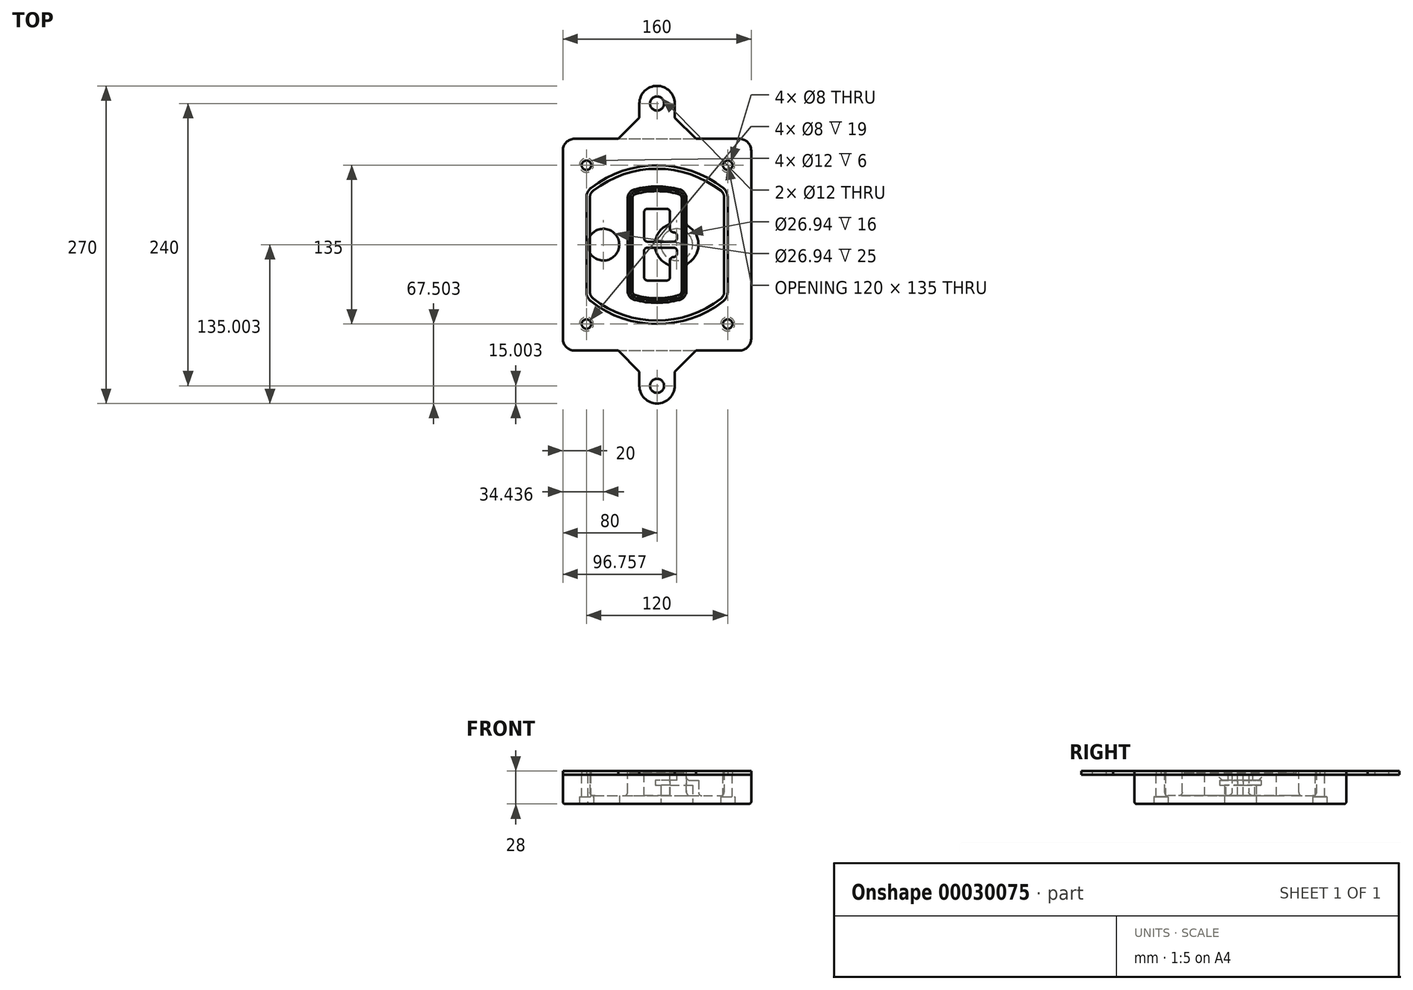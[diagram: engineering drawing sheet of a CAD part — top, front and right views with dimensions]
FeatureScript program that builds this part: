
annotation { "Feature Type Name" : "Feature", "Feature Type Description" : "" }
export const myFeature = defineFeature(function(context is Context, id is Id, definition is map)
    precondition{}
    {
        {
            var Q0;
            Q0=qCreatedBy(makeId("Top.planeOp"),FACE);
            var sketch = newSketch(context, id + "F0", { "sketchPlane" : qUnion([Q0])});
            skPoint(sketch, "E0.rect.middle", {"position": v(0, 0) * mm});
            skLineSegment(sketch, "E1.bottom", {"start": v(24.05, 28.38) * mm, "end": v(164.05, 28.38) * mm});
            skLineSegment(sketch, "E1.top", {"start": v(24.05, 208.38) * mm, "end": v(164.05, 208.38) * mm});
            skLineSegment(sketch, "E1.left", {"start": v(14.05, 38.38) * mm, "end": v(14.05, 198.38) * mm});
            skLineSegment(sketch, "E1.right", {"start": v(174.05, 38.38) * mm, "end": v(174.05, 198.38) * mm});
            skLineSegment(sketch, "E2", {"start": v(14.05, 208.38) * mm, "end": v(174.05, 28.38) * mm, "construction": true});
            skLineSegment(sketch, "E3", {"start": v(174.05, 208.38) * mm, "end": v(14.05, 28.38) * mm, "construction": true});
            skCircle(sketch, "E4", {"center": v(34.05, 185.88) * mm, "radius": 4 * mm});
            skCircle(sketch, "E5", {"center": v(154.05, 185.88) * mm, "radius": 4 * mm});
            skCircle(sketch, "E6", {"center": v(154.05, 50.88) * mm, "radius": 4 * mm});
            skCircle(sketch, "E7", {"center": v(34.05, 50.88) * mm, "radius": 4 * mm});
            skLineSegment(sketch, "E8", {"start": v(34.05, 185.88) * mm, "end": v(154.05, 185.88) * mm, "construction": true});
            skLineSegment(sketch, "E9", {"start": v(154.05, 185.88) * mm, "end": v(154.05, 50.88) * mm, "construction": true});
            skLineSegment(sketch, "E10", {"start": v(154.05, 50.88) * mm, "end": v(34.05, 50.88) * mm, "construction": true});
            skLineSegment(sketch, "E11", {"start": v(34.05, 50.88) * mm, "end": v(34.05, 185.88) * mm, "construction": true});
            skLineSegment(sketch, "E12", {"start": v(34.05, 158.68) * mm, "end": v(34.05, 78.09) * mm});
            skLineSegment(sketch, "E13", {"start": v(154.05, 158.68) * mm, "end": v(154.05, 78.09) * mm});
            skArc(sketch, "E14", {"start": v(150.2, 166.56) * mm, "mid": v(94.05, 185.88) * mm, "end": v(37.9, 166.56) * mm});
            skArc(sketch, "E15", {"start": v(37.9, 70.2) * mm, "mid": v(94.05, 50.88) * mm, "end": v(150.2, 70.2) * mm});
            skLineSegment(sketch, "E16", {"start": v(34.05, 118.38) * mm, "end": v(154.05, 118.38) * mm, "construction": true});
            skPoint(sketch, "E17.visualSharp", {"position": v(34.05, 73.38) * mm});
            skArc(sketch, "E17.filletArc", {"start": v(34.05, 78.09) * mm, "mid": v(35.06, 73.7) * mm, "end": v(37.9, 70.2) * mm});
            skPoint(sketch, "E18.visualSharp", {"position": v(34.05, 163.38) * mm});
            skArc(sketch, "E18.filletArc", {"start": v(37.9, 166.56) * mm, "mid": v(35.06, 163.06) * mm, "end": v(34.05, 158.68) * mm});
            skPoint(sketch, "E19.visualSharp", {"position": v(154.05, 163.38) * mm});
            skArc(sketch, "E19.filletArc", {"start": v(154.05, 158.68) * mm, "mid": v(153.04, 163.06) * mm, "end": v(150.2, 166.56) * mm});
            skPoint(sketch, "E20.visualSharp", {"position": v(154.05, 73.38) * mm});
            skArc(sketch, "E20.filletArc", {"start": v(150.2, 70.2) * mm, "mid": v(153.04, 73.7) * mm, "end": v(154.05, 78.09) * mm});
            skPoint(sketch, "E21.visualSharp", {"position": v(14.05, 208.38) * mm});
            skArc(sketch, "E21.filletArc", {"start": v(24.05, 208.38) * mm, "mid": v(16.98, 205.45) * mm, "end": v(14.05, 198.38) * mm});
            skPoint(sketch, "E22.visualSharp", {"position": v(174.05, 208.38) * mm});
            skArc(sketch, "E22.filletArc", {"start": v(174.05, 198.38) * mm, "mid": v(171.12, 205.45) * mm, "end": v(164.05, 208.38) * mm});
            skPoint(sketch, "E23.visualSharp", {"position": v(174.05, 28.38) * mm});
            skArc(sketch, "E23.filletArc", {"start": v(164.05, 28.38) * mm, "mid": v(171.12, 31.31) * mm, "end": v(174.05, 38.38) * mm});
            skPoint(sketch, "E24.visualSharp", {"position": v(14.05, 28.38) * mm});
            skArc(sketch, "E24.filletArc", {"start": v(14.05, 38.38) * mm, "mid": v(16.98, 31.31) * mm, "end": v(24.05, 28.38) * mm});
            skArc(sketch, "E25.0", {"start": v(151.05, 158.68) * mm, "mid": v(150.34, 161.75) * mm, "end": v(148.36, 164.2) * mm});
            skLineSegment(sketch, "E25.1", {"start": v(151.05, 158.68) * mm, "end": v(151.05, 78.09) * mm});
            skArc(sketch, "E25.2", {"start": v(148.36, 72.57) * mm, "mid": v(150.34, 75.02) * mm, "end": v(151.05, 78.09) * mm});
            skArc(sketch, "E25.3", {"start": v(39.74, 72.57) * mm, "mid": v(94.05, 53.88) * mm, "end": v(148.36, 72.57) * mm});
            skArc(sketch, "E25.4", {"start": v(37.05, 78.09) * mm, "mid": v(37.76, 75.02) * mm, "end": v(39.74, 72.57) * mm});
            skArc(sketch, "E25.5", {"start": v(148.36, 164.2) * mm, "mid": v(94.05, 182.88) * mm, "end": v(39.74, 164.2) * mm});
            skLineSegment(sketch, "E25.6", {"start": v(37.05, 158.68) * mm, "end": v(37.05, 78.09) * mm});
            skArc(sketch, "E25.7", {"start": v(39.74, 164.2) * mm, "mid": v(37.76, 161.75) * mm, "end": v(37.05, 158.68) * mm});
            skArc(sketch, "E26.0", {"start": v(35.43, 169.71) * mm, "mid": v(31.47, 164.82) * mm, "end": v(30.05, 158.68) * mm});
            skArc(sketch, "E26.1", {"start": v(152.67, 169.71) * mm, "mid": v(94.05, 189.88) * mm, "end": v(35.43, 169.71) * mm});
            skArc(sketch, "E26.2", {"start": v(158.05, 158.68) * mm, "mid": v(156.63, 164.82) * mm, "end": v(152.67, 169.71) * mm});
            skLineSegment(sketch, "E26.3", {"start": v(158.05, 158.68) * mm, "end": v(158.05, 78.09) * mm});
            skArc(sketch, "E26.4", {"start": v(152.67, 67.05) * mm, "mid": v(156.63, 71.95) * mm, "end": v(158.05, 78.09) * mm});
            skLineSegment(sketch, "E26.5", {"start": v(30.05, 158.68) * mm, "end": v(30.05, 78.09) * mm});
            skArc(sketch, "E26.6", {"start": v(35.43, 67.05) * mm, "mid": v(94.05, 46.88) * mm, "end": v(152.67, 67.05) * mm});
            skArc(sketch, "E26.7", {"start": v(30.05, 78.09) * mm, "mid": v(31.47, 71.95) * mm, "end": v(35.43, 67.05) * mm});
            skSolve(sketch);
        }
        {
            var Q0;
            Q0=makeQuery(id+"F0.imprint","IMPRINT",FACE,{"disambiguationData":[TD([[makeQuery(id+"F0.imprint","IMPRINT",EDGE,{"derivedFrom":sQuery(id+"F0.wireOp",EDGE,"E1.bottom")}),1.0]])]});
            var Q1;
            Q1=makeQuery(id+"F0.imprint","IMPRINT",FACE,{"disambiguationData":[TD([[makeQuery(id+"F0.imprint","IMPRINT",EDGE,{"derivedFrom":sQuery(id+"F0.wireOp",EDGE,"E12")}),1.0]])]});
            var Q2;
            Q2=makeQuery(id+"F0.imprint","IMPRINT",FACE,{"disambiguationData":[TD([[makeQuery(id+"F0.imprint","IMPRINT",EDGE,{"derivedFrom":sQuery(id+"F0.wireOp",EDGE,"E25.0")}),1.0]])]});
            var Q3;
            Q3=makeQuery(id+"F0.imprint","IMPRINT",FACE,{"disambiguationData":[TD([[makeQuery(id+"F0.imprint","IMPRINT",EDGE,{"derivedFrom":sQuery(id+"F0.wireOp",EDGE,"E12")}),-1.0]])]});
            extrude(context, id + "F1", {"entities" : qUnion([Q0, Q1, Q2, Q3]), "oppositeDirection" : true, "depth" : 25 * mm});
        }
        {
            var Q0;
            Q0=makeQuery(id+"F0.imprint","IMPRINT",FACE,{"disambiguationData":[TD([[makeQuery(id+"F0.imprint","IMPRINT",EDGE,{"derivedFrom":sQuery(id+"F0.wireOp",EDGE,"E12")}),1.0]])]});
            extrude(context, id + "F2", {"entities" : qUnion([Q0]), "operationType" : NewBodyOperationType.ADD, "depth" : 3 * mm});
        }
        {
            var Q0;
            Q0=makeQuery(id+"F0.imprint","IMPRINT",FACE,{"disambiguationData":[TD([[makeQuery(id+"F0.imprint","IMPRINT",EDGE,{"derivedFrom":sQuery(id+"F0.wireOp",EDGE,"E25.0")}),1.0]])]});
            extrude(context, id + "F3", {"entities" : qUnion([Q0]), "operationType" : NewBodyOperationType.REMOVE, "oppositeDirection" : true, "depth" : 18 * mm});
        }
        {
            var Q0;
            Q0=makeQuery(id+"F2.opExtrude","CAP_FACE",FACE,{"disambiguationData":[OSD([sQuery(id+"F0.wireOp",EDGE,"E12"),sQuery(id+"F0.wireOp",EDGE,"E13"),sQuery(id+"F0.wireOp",EDGE,"E14"),sQuery(id+"F0.wireOp",EDGE,"E15"),sQuery(id+"F0.wireOp",EDGE,"E17.filletArc"),sQuery(id+"F0.wireOp",EDGE,"E18.filletArc"),sQuery(id+"F0.wireOp",EDGE,"E19.filletArc"),sQuery(id+"F0.wireOp",EDGE,"E20.filletArc"),sQuery(id+"F0.wireOp",EDGE,"E25.0"),sQuery(id+"F0.wireOp",EDGE,"E25.1"),sQuery(id+"F0.wireOp",EDGE,"E25.2"),sQuery(id+"F0.wireOp",EDGE,"E25.3"),sQuery(id+"F0.wireOp",EDGE,"E25.4"),sQuery(id+"F0.wireOp",EDGE,"E25.5"),sQuery(id+"F0.wireOp",EDGE,"E25.6"),sQuery(id+"F0.wireOp",EDGE,"E25.7")])],"isStart":false});
            var sketch = newSketch(context, id + "F4", { "sketchPlane" : qUnion([Q0])});
            skArc(sketch, "E27.0", {"start": v(74.97, 71.41) * mm, "mid": v(94.05, 68.88) * mm, "end": v(113.13, 71.41) * mm});
            skArc(sketch, "E28.0", {"start": v(113.13, 165.35) * mm, "mid": v(94.05, 167.88) * mm, "end": v(74.97, 165.35) * mm});
            skLineSegment(sketch, "E29", {"start": v(69.05, 157.63) * mm, "end": v(69.05, 79.14) * mm});
            skLineSegment(sketch, "E30", {"start": v(119.05, 157.63) * mm, "end": v(119.05, 79.14) * mm});
            skLineSegment(sketch, "E31", {"start": v(69.05, 163.48) * mm, "end": v(119.05, 163.48) * mm, "construction": true});
            skLineSegment(sketch, "E32", {"start": v(69.05, 73.28) * mm, "end": v(119.05, 73.28) * mm, "construction": true});
            skPoint(sketch, "E33.visualSharp", {"position": v(69.05, 163.48) * mm});
            skArc(sketch, "E33.filletArc", {"start": v(74.97, 165.35) * mm, "mid": v(70.7, 162.5) * mm, "end": v(69.05, 157.63) * mm});
            skPoint(sketch, "E34.visualSharp", {"position": v(119.05, 163.48) * mm});
            skArc(sketch, "E34.filletArc", {"start": v(119.05, 157.63) * mm, "mid": v(117.4, 162.5) * mm, "end": v(113.13, 165.35) * mm});
            skPoint(sketch, "E35.visualSharp", {"position": v(119.05, 73.28) * mm});
            skArc(sketch, "E35.filletArc", {"start": v(113.13, 71.41) * mm, "mid": v(117.4, 74.27) * mm, "end": v(119.05, 79.14) * mm});
            skPoint(sketch, "E36.visualSharp", {"position": v(69.05, 73.28) * mm});
            skArc(sketch, "E36.filletArc", {"start": v(69.05, 79.14) * mm, "mid": v(70.7, 74.27) * mm, "end": v(74.97, 71.41) * mm});
            skArc(sketch, "E37.0", {"start": v(148.36, 164.2) * mm, "mid": v(94.05, 182.88) * mm, "end": v(39.74, 164.2) * mm});
            skArc(sketch, "E37.1", {"start": v(39.74, 164.2) * mm, "mid": v(37.76, 161.75) * mm, "end": v(37.05, 158.68) * mm});
            skLineSegment(sketch, "E37.2", {"start": v(37.05, 158.68) * mm, "end": v(37.05, 78.09) * mm});
            skArc(sketch, "E37.3", {"start": v(37.05, 78.09) * mm, "mid": v(37.76, 75.02) * mm, "end": v(39.74, 72.57) * mm});
            skArc(sketch, "E37.4", {"start": v(39.74, 72.57) * mm, "mid": v(94.05, 53.88) * mm, "end": v(148.36, 72.57) * mm});
            skArc(sketch, "E37.5", {"start": v(148.36, 72.57) * mm, "mid": v(150.34, 75.02) * mm, "end": v(151.05, 78.09) * mm});
            skLineSegment(sketch, "E37.6", {"start": v(151.05, 158.68) * mm, "end": v(151.05, 78.09) * mm});
            skArc(sketch, "E37.7", {"start": v(151.05, 158.68) * mm, "mid": v(150.34, 161.75) * mm, "end": v(148.36, 164.2) * mm});
            skLineSegment(sketch, "E38.0", {"start": v(117.05, 157.63) * mm, "end": v(117.05, 79.14) * mm});
            skArc(sketch, "E38.1", {"start": v(112.61, 73.34) * mm, "mid": v(115.81, 75.49) * mm, "end": v(117.05, 79.14) * mm});
            skArc(sketch, "E38.2", {"start": v(75.49, 73.34) * mm, "mid": v(94.05, 70.88) * mm, "end": v(112.61, 73.34) * mm});
            skArc(sketch, "E38.3", {"start": v(71.05, 79.14) * mm, "mid": v(72.29, 75.49) * mm, "end": v(75.49, 73.34) * mm});
            skLineSegment(sketch, "E38.4", {"start": v(71.05, 157.63) * mm, "end": v(71.05, 79.14) * mm});
            skArc(sketch, "E38.5", {"start": v(117.05, 157.63) * mm, "mid": v(115.81, 161.28) * mm, "end": v(112.61, 163.42) * mm});
            skArc(sketch, "E38.6", {"start": v(75.49, 163.42) * mm, "mid": v(72.29, 161.28) * mm, "end": v(71.05, 157.63) * mm});
            skArc(sketch, "E38.7", {"start": v(112.61, 163.42) * mm, "mid": v(94.05, 165.88) * mm, "end": v(75.49, 163.42) * mm});
            skArc(sketch, "E39.0", {"start": v(115.05, 157.63) * mm, "mid": v(114.23, 160.06) * mm, "end": v(112.1, 161.5) * mm});
            skLineSegment(sketch, "E39.1", {"start": v(115.05, 157.63) * mm, "end": v(115.05, 79.14) * mm});
            skArc(sketch, "E39.2", {"start": v(112.1, 75.27) * mm, "mid": v(114.23, 76.7) * mm, "end": v(115.05, 79.14) * mm});
            skArc(sketch, "E39.3", {"start": v(76, 75.27) * mm, "mid": v(94.05, 72.88) * mm, "end": v(112.1, 75.27) * mm});
            skArc(sketch, "E39.4", {"start": v(73.05, 79.14) * mm, "mid": v(73.87, 76.7) * mm, "end": v(76, 75.27) * mm});
            skArc(sketch, "E39.5", {"start": v(112.1, 161.5) * mm, "mid": v(94.05, 163.88) * mm, "end": v(76, 161.5) * mm});
            skLineSegment(sketch, "E39.6", {"start": v(73.05, 157.63) * mm, "end": v(73.05, 79.14) * mm});
            skArc(sketch, "E39.7", {"start": v(76, 161.5) * mm, "mid": v(73.87, 160.06) * mm, "end": v(73.05, 157.63) * mm});
            skLineSegment(sketch, "E40", {"start": v(69.05, 118.38) * mm, "end": v(119.05, 118.38) * mm, "construction": true});
            skLineSegment(sketch, "E41", {"start": v(83.05, 123.88) * mm, "end": v(83.05, 145.88) * mm});
            skLineSegment(sketch, "E42", {"start": v(86.05, 148.88) * mm, "end": v(102.05, 148.88) * mm});
            skLineSegment(sketch, "E43", {"start": v(105.05, 145.88) * mm, "end": v(105.05, 131.88) * mm});
            skLineSegment(sketch, "E44", {"start": v(108.05, 128.88) * mm, "end": v(108.05, 128.88) * mm});
            skLineSegment(sketch, "E45", {"start": v(111.05, 125.88) * mm, "end": v(111.05, 123.88) * mm});
            skLineSegment(sketch, "E46", {"start": v(108.05, 120.88) * mm, "end": v(86.05, 120.88) * mm});
            skPoint(sketch, "E47.visualSharp", {"position": v(83.05, 148.88) * mm});
            skArc(sketch, "E47.filletArc", {"start": v(86.05, 148.88) * mm, "mid": v(83.93, 148) * mm, "end": v(83.05, 145.88) * mm});
            skPoint(sketch, "E48.visualSharp", {"position": v(105.05, 148.88) * mm});
            skArc(sketch, "E48.filletArc", {"start": v(105.05, 145.88) * mm, "mid": v(104.17, 148) * mm, "end": v(102.05, 148.88) * mm});
            skPoint(sketch, "E49.visualSharp", {"position": v(105.05, 128.88) * mm});
            skArc(sketch, "E49.filletArc", {"start": v(105.05, 131.88) * mm, "mid": v(105.93, 129.76) * mm, "end": v(108.05, 128.88) * mm});
            skPoint(sketch, "E50.visualSharp", {"position": v(111.05, 128.88) * mm});
            skArc(sketch, "E50.filletArc", {"start": v(111.05, 125.88) * mm, "mid": v(110.17, 128) * mm, "end": v(108.05, 128.88) * mm});
            skPoint(sketch, "E51.visualSharp", {"position": v(111.05, 120.88) * mm});
            skArc(sketch, "E51.filletArc", {"start": v(108.05, 120.88) * mm, "mid": v(110.17, 121.76) * mm, "end": v(111.05, 123.88) * mm});
            skPoint(sketch, "E52.visualSharp", {"position": v(83.05, 120.88) * mm});
            skArc(sketch, "E52.filletArc", {"start": v(83.05, 123.88) * mm, "mid": v(83.93, 121.76) * mm, "end": v(86.05, 120.88) * mm});
            skLineSegment(sketch, "E53.0.MirrorCS", {"start": v(108.05, 115.88) * mm, "end": v(86.05, 115.88) * mm});
            skArc(sketch, "E54.0.MirrorCS", {"start": v(83.05, 112.88) * mm, "mid": v(83.93, 115) * mm, "end": v(86.05, 115.88) * mm});
            skLineSegment(sketch, "E55.0.MirrorCS", {"start": v(83.05, 112.88) * mm, "end": v(83.05, 90.88) * mm});
            skArc(sketch, "E56.0.MirrorCS", {"start": v(86.05, 87.88) * mm, "mid": v(83.93, 88.76) * mm, "end": v(83.05, 90.88) * mm});
            skLineSegment(sketch, "E57.0.MirrorCS", {"start": v(86.05, 87.88) * mm, "end": v(102.05, 87.88) * mm});
            skArc(sketch, "E58.0.MirrorCS", {"start": v(105.05, 90.88) * mm, "mid": v(104.17, 88.76) * mm, "end": v(102.05, 87.88) * mm});
            skLineSegment(sketch, "E59.0.MirrorCS", {"start": v(105.05, 90.88) * mm, "end": v(105.05, 104.88) * mm});
            skArc(sketch, "E60.0.MirrorCS", {"start": v(105.05, 104.88) * mm, "mid": v(105.93, 107) * mm, "end": v(108.05, 107.88) * mm});
            skArc(sketch, "E61.0.MirrorCS", {"start": v(111.05, 110.88) * mm, "mid": v(110.17, 108.76) * mm, "end": v(108.05, 107.88) * mm});
            skLineSegment(sketch, "E62.0.MirrorCS", {"start": v(111.05, 110.88) * mm, "end": v(111.05, 112.88) * mm});
            skArc(sketch, "E63.0.MirrorCS", {"start": v(108.05, 115.88) * mm, "mid": v(110.17, 115) * mm, "end": v(111.05, 112.88) * mm});
            skSolve(sketch);
        }
        {
            var Q0;
            Q0=makeQuery(id+"F4.imprint","IMPRINT",FACE,{"disambiguationData":[TD([[makeQuery(id+"F4.imprint","IMPRINT",EDGE,{"derivedFrom":sQuery(id+"F4.wireOp",EDGE,"E27.0")}),1.0]])]});
            var Q1;
            Q1=makeQuery(id+"F4.imprint","IMPRINT",FACE,{"disambiguationData":[TD([[makeQuery(id+"F4.imprint","IMPRINT",EDGE,{"derivedFrom":sQuery(id+"F4.wireOp",EDGE,"E38.0")}),-1.0]])]});
            var Q2;
            Q2=makeQuery(id+"F4.imprint","IMPRINT",FACE,{"disambiguationData":[TD([[makeQuery(id+"F4.imprint","IMPRINT",EDGE,{"derivedFrom":sQuery(id+"F4.wireOp",EDGE,"E39.0")}),1.0]])]});
            extrude(context, id + "F5", {"entities" : qUnion([Q0, Q1, Q2]), "operationType" : NewBodyOperationType.ADD, "endBound" : BoundingType.UP_TO_NEXT, "oppositeDirection" : true, "depth" : 25 * mm});
        }
        {
            var Q0;
            Q0=makeQuery(id+"F4.imprint","IMPRINT",FACE,{"disambiguationData":[TD([[makeQuery(id+"F4.imprint","IMPRINT",EDGE,{"derivedFrom":sQuery(id+"F4.wireOp",EDGE,"E38.0")}),-1.0]])]});
            extrude(context, id + "F6", {"entities" : qUnion([Q0]), "operationType" : NewBodyOperationType.REMOVE, "oppositeDirection" : true, "depth" : 2 * mm});
        }
        {
            var Q0;
            Q0=makeQuery(id+"F1.opExtrude","CAP_FACE",FACE,{"disambiguationData":[OSD([sQuery(id+"F0.wireOp",EDGE,"E1.bottom"),sQuery(id+"F0.wireOp",EDGE,"E1.top"),sQuery(id+"F0.wireOp",EDGE,"E1.left"),sQuery(id+"F0.wireOp",EDGE,"E1.right"),sQuery(id+"F0.wireOp",EDGE,"E4"),sQuery(id+"F0.wireOp",EDGE,"E5"),sQuery(id+"F0.wireOp",EDGE,"E6"),sQuery(id+"F0.wireOp",EDGE,"E7"),sQuery(id+"F0.wireOp",EDGE,"E21.filletArc"),sQuery(id+"F0.wireOp",EDGE,"E22.filletArc"),sQuery(id+"F0.wireOp",EDGE,"E23.filletArc"),sQuery(id+"F0.wireOp",EDGE,"E24.filletArc")])],"isStart":false});
            var sketch = newSketch(context, id + "F7", { "sketchPlane" : qUnion([Q0])});
            skCircle(sketch, "E64", {"center": v(110.8, -118.38) * mm, "radius": 13.47 * mm});
            skCircle(sketch, "E65", {"center": v(48.49, -118.38) * mm, "radius": 13.47 * mm});
            skLineSegment(sketch, "E66", {"start": v(174.05, -118.38) * mm, "end": v(14.05, -118.38) * mm});
            skCircle(sketch, "E67", {"center": v(110.8, -118.38) * mm, "radius": 18.47 * mm});
            skCircle(sketch, "E68", {"center": v(154.05, -185.88) * mm, "radius": 6 * mm});
            skCircle(sketch, "E69", {"center": v(34.05, -185.88) * mm, "radius": 6 * mm});
            skCircle(sketch, "E70", {"center": v(34.05, -50.88) * mm, "radius": 6 * mm});
            skCircle(sketch, "E71", {"center": v(154.05, -50.88) * mm, "radius": 6 * mm});
            skSolve(sketch);
        }
        {
            var Q0;
            {var subQ1=sQuery(id+"F7.wireOp",EDGE,"E66");var subQ4=sQuery(id+"F7.wireOp",EDGE,"E64");var subQ6=makeQuery(id+"F7.imprint","INTERSECT",VERTEX,{"disambiguationData":[OD(0.0)],"derivedFrom":[subQ4,subQ1]});Q0=makeQuery(id+"F7.imprint","IMPRINT",FACE,{"disambiguationData":[TD([[makeQuery(id+"F7.imprint","IMPRINT",EDGE,{"disambiguationData":[TD([[subQ6,-1.0]])],"derivedFrom":subQ4}),-1.0]])]});}
            var Q1;
            {var subQ0=sQuery(id+"F7.wireOp",EDGE,"E66");var subQ1=sQuery(id+"F7.wireOp",EDGE,"E64");var subQ3=makeQuery(id+"F7.imprint","INTERSECT",VERTEX,{"disambiguationData":[OD(0.0)],"derivedFrom":[subQ1,subQ0]});Q1=makeQuery(id+"F7.imprint","IMPRINT",FACE,{"disambiguationData":[TD([[makeQuery(id+"F7.imprint","IMPRINT",EDGE,{"disambiguationData":[TD([[subQ3,-1.0]])],"derivedFrom":subQ1}),1.0]])]});}
            var Q2;
            {var subQ0=sQuery(id+"F7.wireOp",EDGE,"E66");var subQ1=sQuery(id+"F7.wireOp",EDGE,"E64");var subQ3=makeQuery(id+"F7.imprint","INTERSECT",VERTEX,{"disambiguationData":[OD(0.0)],"derivedFrom":[subQ1,subQ0]});Q2=makeQuery(id+"F7.imprint","IMPRINT",FACE,{"disambiguationData":[TD([[makeQuery(id+"F7.imprint","IMPRINT",EDGE,{"disambiguationData":[TD([[subQ3,1.0]])],"derivedFrom":subQ1}),1.0]])]});}
            var Q3;
            {var subQ1=sQuery(id+"F7.wireOp",EDGE,"E66");var subQ4=sQuery(id+"F7.wireOp",EDGE,"E64");var subQ6=makeQuery(id+"F7.imprint","INTERSECT",VERTEX,{"disambiguationData":[OD(0.0)],"derivedFrom":[subQ4,subQ1]});Q3=makeQuery(id+"F7.imprint","IMPRINT",FACE,{"disambiguationData":[TD([[makeQuery(id+"F7.imprint","IMPRINT",EDGE,{"disambiguationData":[TD([[subQ6,1.0]])],"derivedFrom":subQ4}),-1.0]])]});}
            extrude(context, id + "F8", {"entities" : qUnion([Q0, Q1, Q2, Q3]), "operationType" : NewBodyOperationType.ADD, "oppositeDirection" : true, "depth" : 20 * mm});
        }
        {
            var Q0;
            {var subQ0=sQuery(id+"F7.wireOp",EDGE,"E66");var subQ1=sQuery(id+"F7.wireOp",EDGE,"E64");var subQ3=makeQuery(id+"F7.imprint","INTERSECT",VERTEX,{"disambiguationData":[OD(0.0)],"derivedFrom":[subQ1,subQ0]});Q0=makeQuery(id+"F7.imprint","IMPRINT",FACE,{"disambiguationData":[TD([[makeQuery(id+"F7.imprint","IMPRINT",EDGE,{"disambiguationData":[TD([[subQ3,-1.0]])],"derivedFrom":subQ1}),1.0]])]});}
            var Q1;
            {var subQ0=sQuery(id+"F7.wireOp",EDGE,"E66");var subQ1=sQuery(id+"F7.wireOp",EDGE,"E64");var subQ3=makeQuery(id+"F7.imprint","INTERSECT",VERTEX,{"disambiguationData":[OD(0.0)],"derivedFrom":[subQ1,subQ0]});Q1=makeQuery(id+"F7.imprint","IMPRINT",FACE,{"disambiguationData":[TD([[makeQuery(id+"F7.imprint","IMPRINT",EDGE,{"disambiguationData":[TD([[subQ3,1.0]])],"derivedFrom":subQ1}),1.0]])]});}
            extrude(context, id + "F9", {"entities" : qUnion([Q0, Q1]), "operationType" : NewBodyOperationType.REMOVE, "oppositeDirection" : true, "depth" : 16 * mm});
        }
        {
            var Q0;
            {var subQ0=sQuery(id+"F7.wireOp",EDGE,"E66");var subQ1=sQuery(id+"F7.wireOp",EDGE,"E65");var subQ3=makeQuery(id+"F7.imprint","INTERSECT",VERTEX,{"disambiguationData":[OD(0.0)],"derivedFrom":[subQ1,subQ0]});Q0=makeQuery(id+"F7.imprint","IMPRINT",FACE,{"disambiguationData":[TD([[makeQuery(id+"F7.imprint","IMPRINT",EDGE,{"disambiguationData":[TD([[subQ3,-1.0]])],"derivedFrom":subQ1}),1.0]])]});}
            var Q1;
            {var subQ0=sQuery(id+"F7.wireOp",EDGE,"E66");var subQ1=sQuery(id+"F7.wireOp",EDGE,"E65");var subQ3=makeQuery(id+"F7.imprint","INTERSECT",VERTEX,{"disambiguationData":[OD(0.0)],"derivedFrom":[subQ1,subQ0]});Q1=makeQuery(id+"F7.imprint","IMPRINT",FACE,{"disambiguationData":[TD([[makeQuery(id+"F7.imprint","IMPRINT",EDGE,{"disambiguationData":[TD([[subQ3,1.0]])],"derivedFrom":subQ1}),1.0]])]});}
            extrude(context, id + "F10", {"entities" : qUnion([Q0, Q1]), "operationType" : NewBodyOperationType.REMOVE, "oppositeDirection" : true, "depth" : 25 * mm});
        }
        {
            var Q0;
            Q0=makeQuery(id+"F7.imprint","IMPRINT",FACE,{"disambiguationData":[TD([[makeQuery(id+"F7.imprint","IMPRINT",EDGE,{"derivedFrom":sQuery(id+"F7.wireOp",EDGE,"E68")}),1.0]])]});
            var Q1;
            Q1=makeQuery(id+"F7.imprint","IMPRINT",FACE,{"disambiguationData":[TD([[makeQuery(id+"F7.imprint","IMPRINT",EDGE,{"derivedFrom":makeQuery(id+"F1.opExtrude","CAP_EDGE",EDGE,{"disambiguationData":[OSD([sQuery(id+"F0.wireOp",EDGE,"E5")])],"isStart":false})}),-1.0]])]});
            var Q2;
            Q2=makeQuery(id+"F7.imprint","IMPRINT",FACE,{"disambiguationData":[TD([[makeQuery(id+"F7.imprint","IMPRINT",EDGE,{"derivedFrom":sQuery(id+"F7.wireOp",EDGE,"E69")}),1.0]])]});
            var Q3;
            Q3=makeQuery(id+"F7.imprint","IMPRINT",FACE,{"disambiguationData":[TD([[makeQuery(id+"F7.imprint","IMPRINT",EDGE,{"derivedFrom":makeQuery(id+"F1.opExtrude","CAP_EDGE",EDGE,{"disambiguationData":[OSD([sQuery(id+"F0.wireOp",EDGE,"E4")])],"isStart":false})}),-1.0]])]});
            var Q4;
            Q4=makeQuery(id+"F7.imprint","IMPRINT",FACE,{"disambiguationData":[TD([[makeQuery(id+"F7.imprint","IMPRINT",EDGE,{"derivedFrom":sQuery(id+"F7.wireOp",EDGE,"E70")}),1.0]])]});
            var Q5;
            Q5=makeQuery(id+"F7.imprint","IMPRINT",FACE,{"disambiguationData":[TD([[makeQuery(id+"F7.imprint","IMPRINT",EDGE,{"derivedFrom":makeQuery(id+"F1.opExtrude","CAP_EDGE",EDGE,{"disambiguationData":[OSD([sQuery(id+"F0.wireOp",EDGE,"E7")])],"isStart":false})}),-1.0]])]});
            var Q6;
            Q6=makeQuery(id+"F7.imprint","IMPRINT",FACE,{"disambiguationData":[TD([[makeQuery(id+"F7.imprint","IMPRINT",EDGE,{"derivedFrom":sQuery(id+"F7.wireOp",EDGE,"E71")}),1.0]])]});
            var Q7;
            Q7=makeQuery(id+"F7.imprint","IMPRINT",FACE,{"disambiguationData":[TD([[makeQuery(id+"F7.imprint","IMPRINT",EDGE,{"derivedFrom":makeQuery(id+"F1.opExtrude","CAP_EDGE",EDGE,{"disambiguationData":[OSD([sQuery(id+"F0.wireOp",EDGE,"E6")])],"isStart":false})}),-1.0]])]});
            extrude(context, id + "F11", {"entities" : qUnion([Q0, Q1, Q2, Q3, Q4, Q5, Q6, Q7]), "operationType" : NewBodyOperationType.REMOVE, "oppositeDirection" : true, "depth" : 6 * mm});
        }
        {
            var Q0;
            Q0=makeQuery(id+"F9.boolean.opBoolean","COPY",FACE,{"derivedFrom":makeQuery(id+"F9.opExtrude","CAP_FACE",FACE,{"disambiguationData":[OSD([sQuery(id+"F7.wireOp",EDGE,"E64")])],"isStart":false})});
            var sketch = newSketch(context, id + "F12", { "sketchPlane" : qUnion([Q0])});
            skArc(sketch, "E72.0", {"start": v(105.05, -100.83) * mm, "mid": v(96.62, -106.56) * mm, "end": v(92.5, -115.88) * mm});
            skArc(sketch, "E72.1", {"start": v(92.5, -120.88) * mm, "mid": v(96.62, -130.2) * mm, "end": v(105.05, -135.93) * mm});
            skLineSegment(sketch, "E73", {"start": v(92.5, -120.88) * mm, "end": v(108.05, -120.88) * mm});
            skLineSegment(sketch, "E74.0", {"start": v(108.05, -115.88) * mm, "end": v(92.5, -115.88) * mm});
            skArc(sketch, "E74.1", {"start": v(108.05, -115.88) * mm, "mid": v(110.17, -115) * mm, "end": v(111.05, -112.88) * mm});
            skLineSegment(sketch, "E74.2", {"start": v(111.05, -110.88) * mm, "end": v(111.05, -112.88) * mm});
            skArc(sketch, "E74.3", {"start": v(111.05, -110.88) * mm, "mid": v(110.17, -108.76) * mm, "end": v(108.05, -107.88) * mm});
            skArc(sketch, "E74.4", {"start": v(105.05, -104.88) * mm, "mid": v(105.93, -107) * mm, "end": v(108.05, -107.88) * mm});
            skLineSegment(sketch, "E74.5", {"start": v(105.05, -100.83) * mm, "end": v(105.05, -104.88) * mm});
            skLineSegment(sketch, "E74.7", {"start": v(108.05, -120.88) * mm, "end": v(92.5, -120.88) * mm});
            skArc(sketch, "E74.8", {"start": v(108.05, -120.88) * mm, "mid": v(110.17, -121.76) * mm, "end": v(111.05, -123.88) * mm});
            skLineSegment(sketch, "E74.9", {"start": v(111.05, -125.88) * mm, "end": v(111.05, -123.88) * mm});
            skArc(sketch, "E74.10", {"start": v(111.05, -125.88) * mm, "mid": v(110.17, -128) * mm, "end": v(108.05, -128.88) * mm});
            skArc(sketch, "E74.11", {"start": v(105.05, -131.88) * mm, "mid": v(105.93, -129.76) * mm, "end": v(108.05, -128.88) * mm});
            skLineSegment(sketch, "E74.12", {"start": v(105.05, -135.93) * mm, "end": v(105.05, -131.88) * mm});
            skPoint(sketch, "E75.orphan", {"position": v(105.05, -145.88) * mm});
            skPoint(sketch, "E76.orphan", {"position": v(86.05, -120.88) * mm});
            skPoint(sketch, "E77.orphan", {"position": v(86.05, -115.88) * mm});
            skPoint(sketch, "E78.orphan", {"position": v(105.05, -90.88) * mm});
            skSolve(sketch);
        }
        {
            var Q0;
            {var subQ7=sQuery(id+"F12.wireOp",EDGE,"E72.0");var subQ14=sQuery(id+"F12.wireOp",EDGE,"E72.1");var subQ16=sQuery(id+"F12.wireOp",EDGE,"E74.1");var subQ18=sQuery(id+"F12.wireOp",EDGE,"E74.8");Q0=qUnion([makeQuery(id+"F12.imprint","IMPRINT",FACE,{"disambiguationData":[TD([[makeQuery(id+"F12.imprint","IMPRINT",EDGE,{"derivedFrom":subQ7}),1.0]])]}),makeQuery(id+"F12.imprint","IMPRINT",FACE,{"disambiguationData":[TD([[makeQuery(id+"F12.imprint","IMPRINT",EDGE,{"derivedFrom":subQ14}),1.0]])]}),makeQuery(id+"F12.imprint","IMPRINT",FACE,{"disambiguationData":[TD([[makeQuery(id+"F12.imprint","IMPRINT",EDGE,{"derivedFrom":subQ16}),1.0]])]}),makeQuery(id+"F12.imprint","IMPRINT",FACE,{"disambiguationData":[TD([[makeQuery(id+"F12.imprint","IMPRINT",EDGE,{"derivedFrom":subQ18}),-1.0]])]})]);}
            var Q1;
            Q1=makeQuery(id+"F5.boolean.opBoolean","SPLIT",FACE,{"disambiguationData":[TD([makeQuery(id+"F5.opExtrude","SWEPT_FACE",FACE,{"disambiguationData":[OSD([sQuery(id+"F4.wireOp",EDGE,"E41")])]})])],"derivedFrom":makeQuery(id+"F3.boolean.opBoolean","COPY",FACE,{"derivedFrom":makeQuery(id+"F3.opExtrude","CAP_FACE",FACE,{"disambiguationData":[OSD([sQuery(id+"F0.wireOp",EDGE,"E25.0"),sQuery(id+"F0.wireOp",EDGE,"E25.1"),sQuery(id+"F0.wireOp",EDGE,"E25.2"),sQuery(id+"F0.wireOp",EDGE,"E25.3"),sQuery(id+"F0.wireOp",EDGE,"E25.4"),sQuery(id+"F0.wireOp",EDGE,"E25.5"),sQuery(id+"F0.wireOp",EDGE,"E25.6"),sQuery(id+"F0.wireOp",EDGE,"E25.7")])],"isStart":false})})});
            extrude(context, id + "F13", {"entities" : qUnion([Q0]), "operationType" : NewBodyOperationType.REMOVE, "endBound" : BoundingType.UP_TO_SURFACE, "endBoundEntityFace" : qUnion([Q1]), "depth" : 25 * mm});
        }
        {
            var Q0;
            Q0=makeQuery(id+"F3.boolean.opBoolean","COPY",EDGE,{"derivedFrom":makeQuery(id+"F3.opExtrude","CAP_EDGE",EDGE,{"disambiguationData":[OSD([sQuery(id+"F0.wireOp",EDGE,"E25.6")])],"isStart":false})});
            var Q1;
            Q1=makeQuery(id+"F8.boolean.opBoolean","INTERSECT",EDGE,{"derivedFrom":[makeQuery(id+"F5.opExtrude","SWEPT_FACE",FACE,{"disambiguationData":[OSD([sQuery(id+"F4.wireOp",EDGE,"E30")])]}),makeQuery(id+"F8.opExtrude","CAP_FACE",FACE,{"disambiguationData":[OSD([sQuery(id+"F7.wireOp",EDGE,"E67")])],"isStart":false})]});
            var Q2;
            Q2=makeQuery(id+"F8.boolean.opBoolean","INTERSECT",EDGE,{"disambiguationData":[OD(1.0)],"derivedFrom":[makeQuery(id+"F5.opExtrude","SWEPT_FACE",FACE,{"disambiguationData":[OSD([sQuery(id+"F4.wireOp",EDGE,"E30")])]}),makeQuery(id+"F8.opExtrude","SWEPT_FACE",FACE,{"disambiguationData":[OSD([sQuery(id+"F7.wireOp",EDGE,"E67")])]})]});
            var Q3;
            {var subQ0=sQuery(id+"F4.wireOp",EDGE,"E30");Q3=makeQuery(id+"F8.boolean.opBoolean","SPLIT",EDGE,{"disambiguationData":[TD([makeQuery(id+"F5.opExtrude","SWEPT_FACE",FACE,{"disambiguationData":[OSD([sQuery(id+"F4.wireOp",EDGE,"E35.filletArc")])]})])],"derivedFrom":makeQuery(id+"F5.opExtrude","CAP_EDGE",EDGE,{"disambiguationData":[OSD([subQ0])],"isStart":false})});}
            var Q4;
            {var subQ0=sQuery(id+"F0.wireOp",EDGE,"E25.7");var subQ1=sQuery(id+"F0.wireOp",EDGE,"E25.1");var subQ2=sQuery(id+"F0.wireOp",EDGE,"E25.6");var subQ3=sQuery(id+"F0.wireOp",EDGE,"E25.5");var subQ4=sQuery(id+"F0.wireOp",EDGE,"E25.4");var subQ5=sQuery(id+"F0.wireOp",EDGE,"E25.0");var subQ6=sQuery(id+"F0.wireOp",EDGE,"E25.2");var subQ7=sQuery(id+"F0.wireOp",EDGE,"E25.3");Q4=makeQuery(id+"F8.boolean.opBoolean","INTERSECT",EDGE,{"derivedFrom":[makeQuery(id+"F5.boolean.opBoolean","SPLIT",FACE,{"disambiguationData":[TD([makeQuery(id+"F2.opExtrude","SWEPT_FACE",FACE,{"disambiguationData":[OSD([subQ5])]})])],"derivedFrom":makeQuery(id+"F3.boolean.opBoolean","COPY",FACE,{"derivedFrom":makeQuery(id+"F3.opExtrude","CAP_FACE",FACE,{"disambiguationData":[OSD([subQ5,subQ1,subQ6,subQ7,subQ4,subQ3,subQ2,subQ0])],"isStart":false})})}),makeQuery(id+"F8.opExtrude","SWEPT_FACE",FACE,{"disambiguationData":[OSD([sQuery(id+"F7.wireOp",EDGE,"E67")])]})]});}
            var Q5;
            Q5=makeQuery(id+"F8.boolean.opBoolean","INTERSECT",EDGE,{"disambiguationData":[OD(0.0)],"derivedFrom":[makeQuery(id+"F5.opExtrude","SWEPT_FACE",FACE,{"disambiguationData":[OSD([sQuery(id+"F4.wireOp",EDGE,"E30")])]}),makeQuery(id+"F8.opExtrude","SWEPT_FACE",FACE,{"disambiguationData":[OSD([sQuery(id+"F7.wireOp",EDGE,"E67")])]})]});
            fillet(context, id + "F14", {"entities" : qUnion([Q0, Q1, Q2, Q3, Q4, Q5]), "radius" : 3 * mm, "tangentPropagation" : true, "allowEdgeOverflow" : false});
        }
        {
            var Q0;
            Q0=makeQuery(id+"F1.opExtrude","CAP_EDGE",EDGE,{"disambiguationData":[OSD([sQuery(id+"F0.wireOp",EDGE,"E1.bottom")])],"isStart":false});
            fillet(context, id + "F15", {"entities" : qUnion([Q0]), "radius" : 2 * mm, "tangentPropagation" : true, "allowEdgeOverflow" : false});
        }
        {
            var Q0;
            {var subQ0=sQuery(id+"F0.wireOp",EDGE,"E1.bottom");var subQ1=sQuery(id+"F0.wireOp",EDGE,"E1.top");var subQ2=sQuery(id+"F0.wireOp",EDGE,"E1.left");var subQ3=sQuery(id+"F0.wireOp",EDGE,"E1.right");var subQ4=sQuery(id+"F0.wireOp",EDGE,"E4");var subQ5=sQuery(id+"F0.wireOp",EDGE,"E5");var subQ6=sQuery(id+"F0.wireOp",EDGE,"E6");var subQ7=sQuery(id+"F0.wireOp",EDGE,"E7");var subQ8=sQuery(id+"F0.wireOp",EDGE,"E21.filletArc");var subQ9=sQuery(id+"F0.wireOp",EDGE,"E22.filletArc");var subQ10=sQuery(id+"F0.wireOp",EDGE,"E23.filletArc");var subQ11=sQuery(id+"F0.wireOp",EDGE,"E24.filletArc");Q0=makeQuery(id+"F2.boolean.opBoolean","SPLIT",FACE,{"disambiguationData":[TD([makeQuery(id+"F1.opExtrude","SWEPT_FACE",FACE,{"disambiguationData":[OSD([subQ0])]})])],"derivedFrom":makeQuery(id+"F1.opExtrude","CAP_FACE",FACE,{"disambiguationData":[OSD([subQ0,subQ1,subQ2,subQ3,subQ4,subQ5,subQ6,subQ7,subQ8,subQ9,subQ10,subQ11])],"isStart":true})});}
            var sketch = newSketch(context, id + "F16", { "sketchPlane" : qUnion([Q0])});
            skLineSegment(sketch, "E79.0", {"start": v(24.05, 208.38) * mm, "end": v(164.05, 208.38) * mm});
            skArc(sketch, "E79.1", {"start": v(174.05, 198.38) * mm, "mid": v(171.12, 205.45) * mm, "end": v(164.05, 208.38) * mm});
            skLineSegment(sketch, "E79.2", {"start": v(174.05, 38.38) * mm, "end": v(174.05, 198.38) * mm});
            skArc(sketch, "E79.3", {"start": v(164.05, 28.38) * mm, "mid": v(171.12, 31.31) * mm, "end": v(174.05, 38.38) * mm});
            skLineSegment(sketch, "E79.4", {"start": v(24.05, 28.38) * mm, "end": v(164.05, 28.38) * mm});
            skArc(sketch, "E79.5", {"start": v(14.05, 38.38) * mm, "mid": v(16.98, 31.31) * mm, "end": v(24.05, 28.38) * mm});
            skLineSegment(sketch, "E79.6", {"start": v(14.05, 38.38) * mm, "end": v(14.05, 198.38) * mm});
            skArc(sketch, "E79.7", {"start": v(24.05, 208.38) * mm, "mid": v(16.98, 205.45) * mm, "end": v(14.05, 198.38) * mm});
            skCircle(sketch, "E79.8", {"center": v(34.05, 185.88) * mm, "radius": 4 * mm});
            skCircle(sketch, "E79.9", {"center": v(154.05, 185.88) * mm, "radius": 4 * mm});
            skCircle(sketch, "E79.10", {"center": v(154.05, 50.88) * mm, "radius": 4 * mm});
            skCircle(sketch, "E79.11", {"center": v(34.05, 50.88) * mm, "radius": 4 * mm});
            skLineSegment(sketch, "E79.12", {"start": v(154.05, 158.68) * mm, "end": v(154.05, 78.09) * mm});
            skArc(sketch, "E79.13", {"start": v(150.2, 70.2) * mm, "mid": v(153.04, 73.7) * mm, "end": v(154.05, 78.09) * mm});
            skArc(sketch, "E79.14", {"start": v(37.9, 70.2) * mm, "mid": v(94.05, 50.88) * mm, "end": v(150.2, 70.2) * mm});
            skArc(sketch, "E79.15", {"start": v(154.05, 158.68) * mm, "mid": v(153.04, 163.06) * mm, "end": v(150.2, 166.56) * mm});
            skArc(sketch, "E79.16", {"start": v(34.05, 78.09) * mm, "mid": v(35.06, 73.7) * mm, "end": v(37.9, 70.2) * mm});
            skLineSegment(sketch, "E79.17", {"start": v(34.05, 158.68) * mm, "end": v(34.05, 78.09) * mm});
            skArc(sketch, "E79.18", {"start": v(37.9, 166.56) * mm, "mid": v(35.06, 163.06) * mm, "end": v(34.05, 158.68) * mm});
            skArc(sketch, "E79.19", {"start": v(150.2, 166.56) * mm, "mid": v(94.05, 185.88) * mm, "end": v(37.9, 166.56) * mm});
            skLineSegment(sketch, "E80", {"start": v(94.05, 208.38) * mm, "end": v(94.05, 238.38) * mm, "construction": true});
            skCircle(sketch, "E81", {"center": v(94.05, 238.38) * mm, "radius": 6 * mm});
            skLineSegment(sketch, "E82", {"start": v(79.05, 238.38) * mm, "end": v(79.05, 226.38) * mm});
            skLineSegment(sketch, "E83", {"start": v(79.05, 226.38) * mm, "end": v(61.05, 208.38) * mm});
            skLineSegment(sketch, "E84", {"start": v(109.05, 238.38) * mm, "end": v(109.05, 226.38) * mm});
            skLineSegment(sketch, "E85", {"start": v(109.05, 226.38) * mm, "end": v(127.05, 208.38) * mm});
            skArc(sketch, "E86", {"start": v(109.05, 238.38) * mm, "mid": v(94.05, 253.38) * mm, "end": v(79.05, 238.38) * mm});
            skLineSegment(sketch, "E87", {"start": v(14.05, 118.38) * mm, "end": v(174.05, 118.38) * mm, "construction": true});
            skArc(sketch, "E88.MirrorCS", {"start": v(109.05, -1.62) * mm, "mid": v(94.05, -16.62) * mm, "end": v(79.05, -1.62) * mm});
            skCircle(sketch, "E89.MirrorC", {"center": v(94.05, -1.62) * mm, "radius": 6 * mm});
            skLineSegment(sketch, "E90.MirrorCS", {"start": v(109.05, -1.62) * mm, "end": v(109.05, 10.38) * mm});
            skLineSegment(sketch, "E91.MirrorCS", {"start": v(79.05, -1.62) * mm, "end": v(79.05, 10.38) * mm});
            skLineSegment(sketch, "E92.MirrorCS", {"start": v(94.05, 28.38) * mm, "end": v(94.05, -1.62) * mm});
            skLineSegment(sketch, "E93.MirrorCS", {"start": v(109.05, 10.38) * mm, "end": v(127.05, 28.38) * mm});
            skLineSegment(sketch, "E94.MirrorCS", {"start": v(79.05, 10.38) * mm, "end": v(61.05, 28.38) * mm});
            skSolve(sketch);
        }
        {
            var Q0;
            Q0 = qSketchRegion(id + "F16", true);
            var Q1;
            Q1=makeQuery(id+"F2.opExtrude","CAP_FACE",FACE,{"disambiguationData":[OSD([sQuery(id+"F0.wireOp",EDGE,"E12"),sQuery(id+"F0.wireOp",EDGE,"E13"),sQuery(id+"F0.wireOp",EDGE,"E14"),sQuery(id+"F0.wireOp",EDGE,"E15"),sQuery(id+"F0.wireOp",EDGE,"E17.filletArc"),sQuery(id+"F0.wireOp",EDGE,"E18.filletArc"),sQuery(id+"F0.wireOp",EDGE,"E19.filletArc"),sQuery(id+"F0.wireOp",EDGE,"E20.filletArc"),sQuery(id+"F0.wireOp",EDGE,"E25.0"),sQuery(id+"F0.wireOp",EDGE,"E25.1"),sQuery(id+"F0.wireOp",EDGE,"E25.2"),sQuery(id+"F0.wireOp",EDGE,"E25.3"),sQuery(id+"F0.wireOp",EDGE,"E25.4"),sQuery(id+"F0.wireOp",EDGE,"E25.5"),sQuery(id+"F0.wireOp",EDGE,"E25.6"),sQuery(id+"F0.wireOp",EDGE,"E25.7")])],"isStart":false});
            extrude(context, id + "F17", {"entities" : qUnion([Q0]), "endBound" : BoundingType.UP_TO_SURFACE, "endBoundEntityFace" : qUnion([Q1]), "depth" : 25 * mm});
        }
    });
